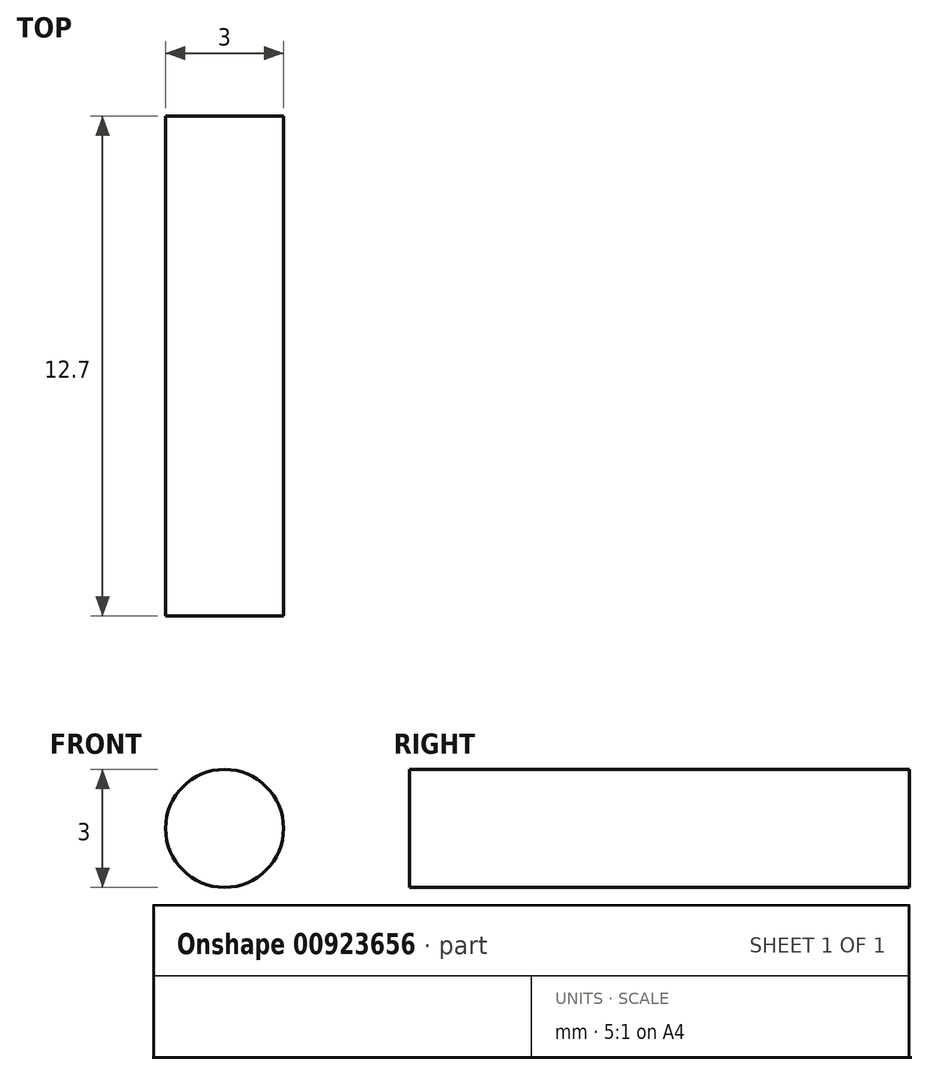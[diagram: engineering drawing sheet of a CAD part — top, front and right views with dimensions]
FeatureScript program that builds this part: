
annotation { "Feature Type Name" : "Feature", "Feature Type Description" : "" }
export const myFeature = defineFeature(function(context is Context, id is Id, definition is map)
    precondition{}
    {
        {
            var Q0;
            Q0=qCreatedBy(makeId("Front.planeOp"),FACE);
            var sketch = newSketch(context, id + "F0", { "sketchPlane" : qUnion([Q0])});
            skCircle(sketch, "E0", {"center": v(0, 0) * mm, "radius": 1.5 * mm});
            skSolve(sketch);
        }
        {
            var Q0;
            Q0 = qSketchRegion(id + "F0", true);
            extrude(context, id + "F1", {"entities" : qUnion([Q0]), "depth" : 12.7 * mm, "offsetDistance" : 25.4 * mm});
        }
    });
